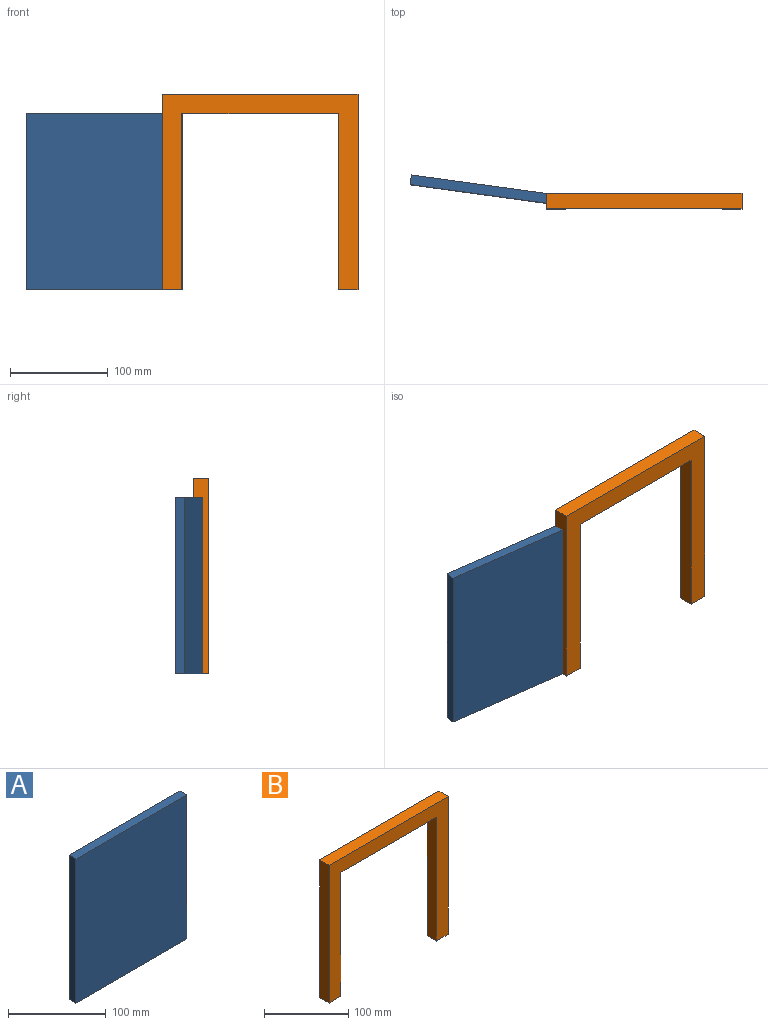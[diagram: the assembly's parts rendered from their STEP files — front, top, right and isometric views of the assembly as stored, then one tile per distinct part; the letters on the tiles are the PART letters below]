
ASSEMBLY  parts=2 mates=1
PART A: 6 faces, bbox 160x9.9x180 mm
  f0: plane 180x9.91mm, normal (-1,0,0), area 1783.1mm2, adj f1,f3,f4,f5
  f1: plane 160x9.91mm, normal (0,0,-1), area 1585mm2, adj f0,f2,f4,f5
  f2: plane 180x9.91mm, normal (1,0,0), area 1783.1mm2, adj f1,f3,f4,f5
  f3: plane 160x9.91mm, normal (0,0,1), area 1585mm2, adj f0,f2,f4,f5
  f4: plane 180x160mm, normal (0,-1,0), area 28800mm2, adj f0,f1,f2,f3
  f5: plane 180x160mm, normal (0,1,0), area 28800mm2, adj f0,f1,f2,f3
PART B: 10 faces, bbox 200x15.7x200 mm
  f0: plane 180x15.75mm, normal (-1,0,0), area 2834.6mm2, adj f1,f7,f8,f9
  f1: plane 20x15.75mm, normal (0,0,-1), area 315mm2, adj f0,f2,f8,f9
  f2: plane 200x15.75mm, normal (1,0,0), area 3149.6mm2, adj f1,f3,f8,f9
  f3: plane 200x15.75mm, normal (0,0,1), area 3149.6mm2, adj f2,f4,f8,f9
  f4: plane 200x15.75mm, normal (-1,0,0), area 3149.6mm2, adj f3,f5,f8,f9
  f5: plane 20x15.75mm, normal (0,0,-1), area 315mm2, adj f4,f6,f8,f9
  f6: plane 180x15.75mm, normal (1,0,0), area 2834.6mm2, adj f5,f7,f8,f9
  f7: plane 160x15.75mm, normal (0,0,-1), area 2519.7mm2, adj f0,f6,f8,f9
  f8: plane 200x200mm, normal (0,-1,0), area 11200mm2, adj f0,f1,f2,f3,f4,f5,f6,f7
  f9: plane 200x200mm, normal (0,1,0), area 11200mm2, adj f0,f1,f2,f3,f4,f5,f6,f7
PLACE A rot(axis=(0,0,1),172.2deg) t=(-1.83,-2.19,-12.9)mm
PLACE B t=(-40.98,13.3,-12.9)mm fixed
MATE revolute B.f7 <-> A.f3  axis (0,0,-1) through (-20.98,5.43,167.1)mm
